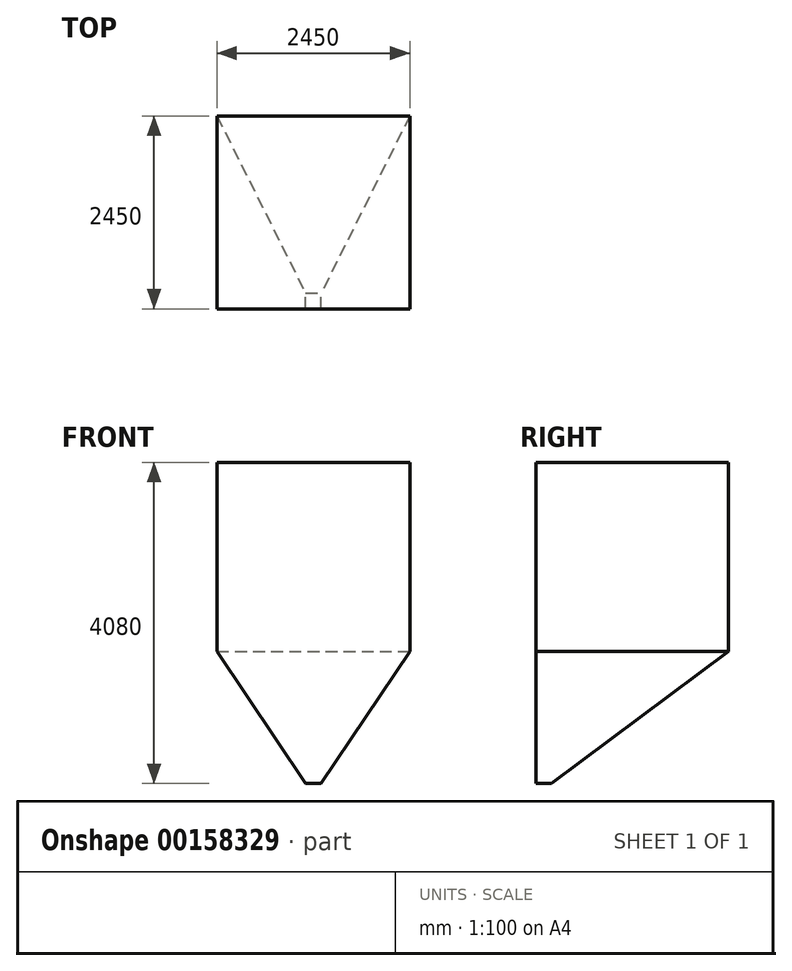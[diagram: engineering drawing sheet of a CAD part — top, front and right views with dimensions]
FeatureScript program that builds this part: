
annotation { "Feature Type Name" : "Feature", "Feature Type Description" : "" }
export const myFeature = defineFeature(function(context is Context, id is Id, definition is map)
    precondition{}
    {
        {
            var Q0;
            Q0=qCreatedBy(makeId("Top.planeOp"),FACE);
            var sketch = newSketch(context, id + "F0", { "sketchPlane" : qUnion([Q0])});
            skLineSegment(sketch, "E0.bottom", {"start": v(-1225, 1225) * mm, "end": v(1225, 1225) * mm});
            skLineSegment(sketch, "E0.top", {"start": v(-1225, -1225) * mm, "end": v(1225, -1225) * mm});
            skLineSegment(sketch, "E0.left", {"start": v(-1225, 1225) * mm, "end": v(-1225, -1225) * mm});
            skLineSegment(sketch, "E0.right", {"start": v(1225, 1225) * mm, "end": v(1225, -1225) * mm});
            skPoint(sketch, "E0.middle", {"position": v(0, 0) * mm});
            skSolve(sketch);
        }
        {
            var Q0;
            Q0=makeQuery(id+"F0.imprint","IMPRINT",FACE,{"disambiguationData":[TD([[makeQuery(id+"F0.imprint","IMPRINT",EDGE,{"derivedFrom":sQuery(id+"F0.wireOp",EDGE,"E0.bottom")}),-1.0]])]});
            extrude(context, id + "F1", {"entities" : qUnion([Q0]), "depth" : 2400 * mm});
        }
        {
            var Q0;
            Q0=makeQuery(id+"F1.opExtrude","CAP_FACE",FACE,{"disambiguationData":[OSD([sQuery(id+"F0.wireOp",EDGE,"E0.bottom"),sQuery(id+"F0.wireOp",EDGE,"E0.top"),sQuery(id+"F0.wireOp",EDGE,"E0.left"),sQuery(id+"F0.wireOp",EDGE,"E0.right")])],"isStart":true});
            cPlane(context, id + "F2", {"entities" : qUnion([Q0]), "cplaneType" : CPlaneType.OFFSET, "offset" : 1680 * mm, "width" : 150 * mm, "height" : 150 * mm});
        }
        {
            var Q0;
            Q0=qCreatedBy(id+"F2.planeOp",FACE);
            var sketch = newSketch(context, id + "F3", { "sketchPlane" : qUnion([Q0])});
            skLineSegment(sketch, "E1.bottom", {"start": v(-100, 1225) * mm, "end": v(100, 1225) * mm});
            skLineSegment(sketch, "E1.top", {"start": v(-100, 1025) * mm, "end": v(100, 1025) * mm});
            skLineSegment(sketch, "E1.left", {"start": v(100, 1225) * mm, "end": v(100, 1025) * mm});
            skLineSegment(sketch, "E1.right", {"start": v(-100, 1225) * mm, "end": v(-100, 1025) * mm});
            skPoint(sketch, "E2", {"position": v(0, 1225) * mm});
            skSolve(sketch);
        }
        {
            var Q1;
            Q1=makeQuery(id+"F1.opExtrude","CAP_FACE",FACE,{"disambiguationData":[OSD([sQuery(id+"F0.wireOp",EDGE,"E0.bottom"),sQuery(id+"F0.wireOp",EDGE,"E0.top"),sQuery(id+"F0.wireOp",EDGE,"E0.left"),sQuery(id+"F0.wireOp",EDGE,"E0.right")])],"isStart":true});
            var Q2;
            Q2=makeQuery(id+"F3.imprint","IMPRINT",FACE,{"disambiguationData":[TD([[makeQuery(id+"F3.imprint","IMPRINT",EDGE,{"derivedFrom":sQuery(id+"F3.wireOp",EDGE,"E1.bottom")}),-1.0]])]});
            loft(context, id + "F4", {"operationType" : NewBodyOperationType.ADD, "sheetProfilesArray" : [{ "sheetProfileEntities" : qUnion([Q1]) }, { "sheetProfileEntities" : qUnion([Q2]) }]});
        }
        {
            var Q0;
            Q0=makeQuery(id+"F1.opExtrude","CAP_FACE",FACE,{"disambiguationData":[OSD([sQuery(id+"F0.wireOp",EDGE,"E0.bottom"),sQuery(id+"F0.wireOp",EDGE,"E0.top"),sQuery(id+"F0.wireOp",EDGE,"E0.left"),sQuery(id+"F0.wireOp",EDGE,"E0.right")])],"isStart":false});
            extrude(context, id + "F5", {"entities" : qUnion([Q0]), "depth" : 400 * mm});
        }
        {
            var Q0;
            Q0=makeQuery(id+"F5.opExtrude","CAP_FACE",FACE,{"disambiguationData":[OSD([sQuery(id+"F0.wireOp",EDGE,"E0.bottom"),sQuery(id+"F0.wireOp",EDGE,"E0.top"),sQuery(id+"F0.wireOp",EDGE,"E0.left"),sQuery(id+"F0.wireOp",EDGE,"E0.right")])],"isStart":false});
            extrude(context, id + "F6", {"entities" : qUnion([Q0]), "depth" : 400 * mm});
        }
        {
            var Q0;
            Q0=makeQuery(id+"F6.opExtrude","SWEPT_BODY",BODY,{"disambiguationData":[OSD([sQuery(id+"F0.wireOp",EDGE,"E0.bottom"),sQuery(id+"F0.wireOp",EDGE,"E0.top"),sQuery(id+"F0.wireOp",EDGE,"E0.left"),sQuery(id+"F0.wireOp",EDGE,"E0.right")])]});
            var Q1;
            Q1=makeQuery(id+"F5.opExtrude","SWEPT_BODY",BODY,{"disambiguationData":[OSD([sQuery(id+"F0.wireOp",EDGE,"E0.bottom"),sQuery(id+"F0.wireOp",EDGE,"E0.top"),sQuery(id+"F0.wireOp",EDGE,"E0.left"),sQuery(id+"F0.wireOp",EDGE,"E0.right")])]});
            deleteBodies(context, id + "F7", {"entities" : qUnion([Q0, Q1])});
        }
    });
